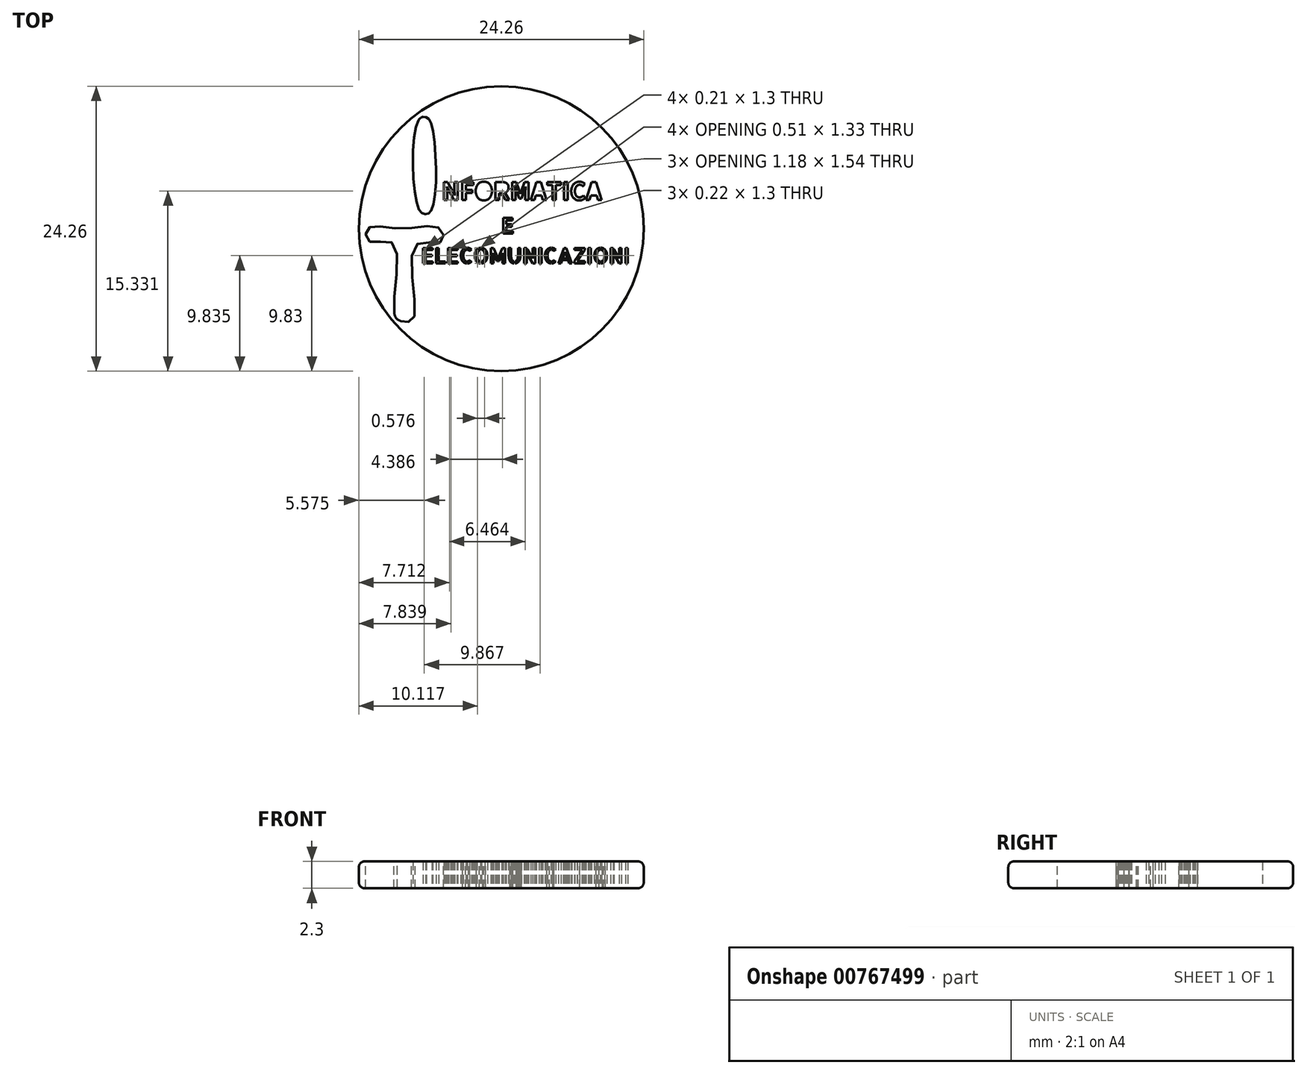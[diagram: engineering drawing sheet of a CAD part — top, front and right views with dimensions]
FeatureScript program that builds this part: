
annotation { "Feature Type Name" : "Feature", "Feature Type Description" : "" }
export const myFeature = defineFeature(function(context is Context, id is Id, definition is map)
    precondition{}
    {
        {
            var Q0;
            Q0=qCreatedBy(makeId("Top.planeOp"),FACE);
            var sketch = newSketch(context, id + "F0", { "sketchPlane" : qUnion([Q0])});
            skCircle(sketch, "E0", {"center": v(0, 0) * mm, "radius": 12.13 * mm});
            skFitSpline(sketch, "E1", {"points": [v(-6.44, 1.23) * mm, v(-5.81, 1.9) * mm, v(-5.94, 8.83) * mm, v(-6.47, 9.51) * mm, v(-7.13, 9.1) * mm, v(-7.1, 1.86) * mm, v(-6.44, 1.23) * mm]});
            skFitSpline(sketch, "E2", {"points": [v(-11.38, 0) * mm, v(-8.53, 0) * mm, v(-5.2, 0) * mm, v(-5.14, -1.13) * mm, v(-7.31, -1.43) * mm, v(-7.43, -7.55) * mm, v(-8.32, -7.91) * mm, v(-9.1, -7.24) * mm, v(-9.2, -1.27) * mm, v(-11.24, -1.1) * mm, v(-11.38, 0) * mm]});
            skText(sketch, "E3", { "text": "NFORMATICA", "fontName": "NotoSansCJKtc-Bold.otf"});
            skText(sketch, "E4", { "text": "ELECOMUNICAZIONI", "fontName": "AllertaStencil-Regular.ttf"});
            skText(sketch, "E5", { "text": "E", "fontName": "NotoSansCJKtc-Bold.otf"});
            const initialGuessF0  = {"E3": [-0.00507, 0.00243, 1, 0, 0.0015], "E4": [-0.00683, -0.00295, 1, 0, 0.0013], "E5": [0, -0.0004, 1, 0, 0.00127]};
            skSetInitialGuess(sketch, initialGuessF0);
            skSolve(sketch);
        }
        {
            var Q0;
            Q0 = qSketchRegion(id + "F0", true);
            extrude(context, id + "F1", {"entities" : qUnion([Q0]), "depth" : 2.3 * mm, "offsetDistance" : 25 * mm});
        }
        {
            var Q0;
            Q0=makeQuery(id+"F1.opExtrude","SWEPT_FACE",FACE,{"disambiguationData":[OSD([sQuery(id+"F0.wireOp",EDGE,"E0")])]});
            fillet(context, id + "F2", {"entities" : qUnion([Q0]), "radius" : 0.5 * mm, "tangentPropagation" : true, "allowEdgeOverflow" : false});
        }
    });
